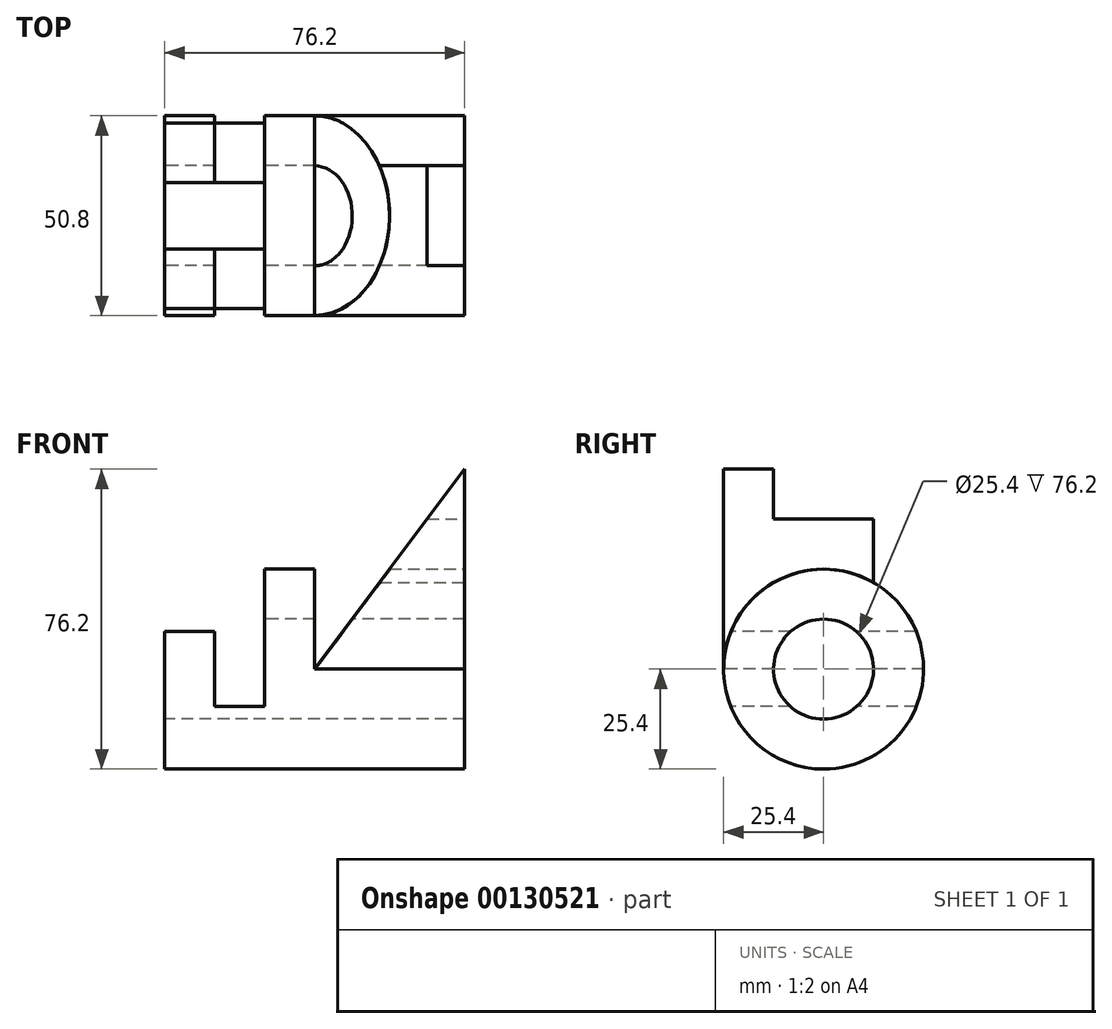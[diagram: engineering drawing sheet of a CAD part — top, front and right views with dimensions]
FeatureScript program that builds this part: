
annotation { "Feature Type Name" : "Feature", "Feature Type Description" : "" }
export const myFeature = defineFeature(function(context is Context, id is Id, definition is map)
    precondition{}
    {
        {
            var Q0;
            Q0=qCreatedBy(makeId("Right.planeOp"),FACE);
            var sketch = newSketch(context, id + "F0", { "sketchPlane" : qUnion([Q0])});
            skCircle(sketch, "E0", {"center": v(0, 0) * mm, "radius": 25.4 * mm});
            skCircle(sketch, "E1", {"center": v(0, 0) * mm, "radius": 12.7 * mm});
            skSolve(sketch);
        }
        {
            var Q0;
            Q0 = qSketchRegion(id + "F0", true);
            extrude(context, id + "F1", {"entities" : qUnion([Q0]), "depth" : 76.2 * mm});
        }
        {
            var Q0;
            Q0=makeQuery(id+"F1.opExtrude","CAP_FACE",FACE,{"disambiguationData":[OSD([sQuery(id+"F0.wireOp",EDGE,"E0"),sQuery(id+"F0.wireOp",EDGE,"E1")])],"isStart":false});
            var sketch = newSketch(context, id + "F2", { "sketchPlane" : qUnion([Q0])});
            skLineSegment(sketch, "E2", {"start": v(12.7, 22) * mm, "end": v(12.7, 38.1) * mm});
            skLineSegment(sketch, "E3", {"start": v(12.7, 38.1) * mm, "end": v(-12.7, 38.1) * mm});
            skLineSegment(sketch, "E4", {"start": v(-12.7, 38.1) * mm, "end": v(-12.7, 50.8) * mm});
            skLineSegment(sketch, "E5", {"start": v(-25.4, 0) * mm, "end": v(-25.4, 50.8) * mm});
            skLineSegment(sketch, "E6", {"start": v(-12.7, 50.8) * mm, "end": v(-25.4, 50.8) * mm});
            skSolve(sketch);
        }
        {
            var Q0;
            Q0 = qSketchRegion(id + "F2", true);
            var Q1;
            {var subQ1=sQuery(id+"F2.wireOp",EDGE,"E2");Q1=makeQuery(id+"F2.imprint","IMPRINT",FACE,{"disambiguationData":[TD([[makeQuery(id+"F2.imprint","IMPRINT",EDGE,{"derivedFrom":subQ1}),1.0]])]});}
            extrude(context, id + "F3", {"entities" : qUnion([Q0, Q1]), "oppositeDirection" : true, "depth" : 38.1 * mm});
        }
        {
            var Q0;
            Q0=makeQuery(id+"F3.opExtrude","SWEPT_FACE",FACE,{"disambiguationData":[OSD([sQuery(id+"F2.wireOp",EDGE,"E5")])]});
            var sketch = newSketch(context, id + "F4", { "sketchPlane" : qUnion([Q0])});
            skLineSegment(sketch, "E7", {"start": v(38.1, 0) * mm, "end": v(76.2, 50.8) * mm});
            skLineSegment(sketch, "E8", {"start": v(76.2, 50.8) * mm, "end": v(38.1, 50.8) * mm});
            skLineSegment(sketch, "E9", {"start": v(38.1, 50.8) * mm, "end": v(38.1, 0) * mm});
            skSolve(sketch);
        }
        {
            var Q0;
            Q0 = qSketchRegion(id + "F4", true);
            extrude(context, id + "F5", {"entities" : qUnion([Q0]), "operationType" : NewBodyOperationType.REMOVE, "endBound" : BoundingType.THROUGH_ALL, "oppositeDirection" : true, "depth" : 25.4 * mm});
        }
        {
            var Q0;
            Q0=qCreatedBy(makeId("Front.planeOp"),FACE);
            var sketch = newSketch(context, id + "F6", { "sketchPlane" : qUnion([Q0])});
            skLineSegment(sketch, "E10", {"start": v(0, 0) * mm, "end": v(0, 25.4) * mm, "construction": true});
            skLineSegment(sketch, "E11", {"start": v(0, 25.4) * mm, "end": v(76.2, 25.4) * mm, "construction": true});
            skLineSegment(sketch, "E12", {"start": v(25.4, 25.4) * mm, "end": v(25.4, -9.52) * mm});
            skLineSegment(sketch, "E13", {"start": v(25.4, -9.52) * mm, "end": v(12.7, -9.52) * mm});
            skLineSegment(sketch, "E14", {"start": v(12.7, -9.52) * mm, "end": v(12.7, 9.53) * mm});
            skLineSegment(sketch, "E15", {"start": v(12.7, 9.53) * mm, "end": v(0, 9.53) * mm});
            skLineSegment(sketch, "E16", {"start": v(0, 9.53) * mm, "end": v(0, 25.4) * mm});
            skLineSegment(sketch, "E17", {"start": v(25.4, 25.4) * mm, "end": v(0, 25.4) * mm});
            skSolve(sketch);
        }
        {
            var Q0;
            Q0 = qSketchRegion(id + "F6", true);
            extrude(context, id + "F7", {"entities" : qUnion([Q0]), "operationType" : NewBodyOperationType.REMOVE, "endBound" : BoundingType.THROUGH_ALL, "oppositeDirection" : true, "depth" : 25.4 * mm, "hasSecondDirection" : true, "secondDirectionBound" : SecondDirectionBoundingType.THROUGH_ALL, "secondDirectionOppositeDirection" : false, "secondDirectionDepth" : 25.4 * mm});
        }
    });
